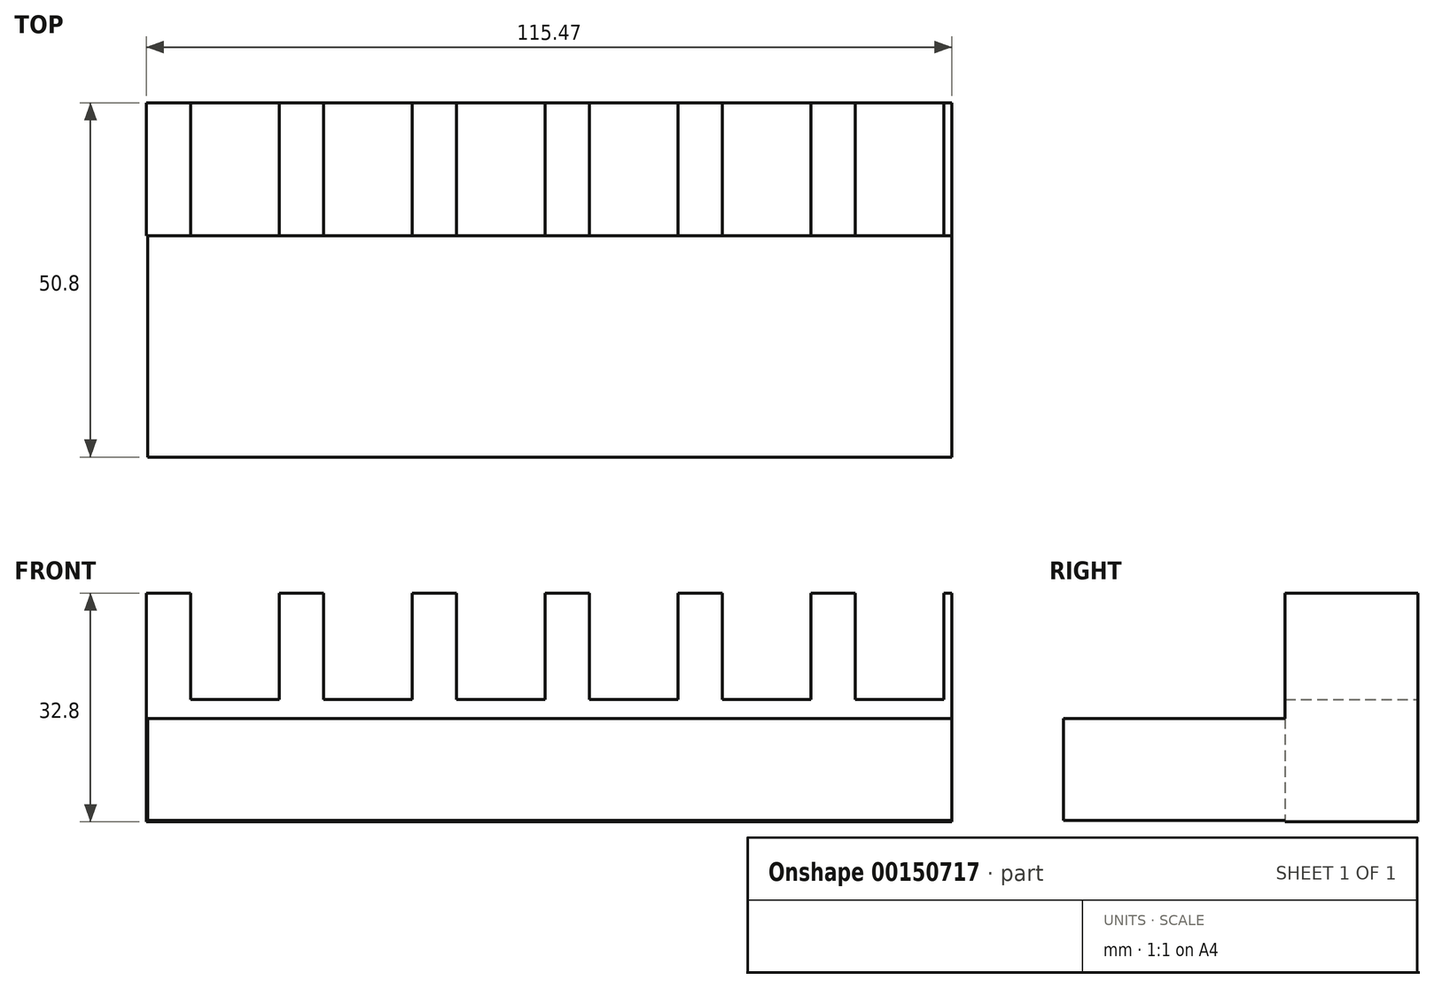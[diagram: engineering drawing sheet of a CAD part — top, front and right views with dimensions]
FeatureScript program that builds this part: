
annotation { "Feature Type Name" : "Feature", "Feature Type Description" : "" }
export const myFeature = defineFeature(function(context is Context, id is Id, definition is map)
    precondition{}
    {
        {
            var Q0;
            Q0=qCreatedBy(makeId("Front.planeOp"),FACE);
            var sketch = newSketch(context, id + "F0", { "sketchPlane" : qUnion([Q0])});
            skLineSegment(sketch, "E0.bottom", {"start": v(-57.62, 2.44) * mm, "end": v(57.85, 2.44) * mm});
            skLineSegment(sketch, "E0.top", {"start": v(-57.62, -30.36) * mm, "end": v(57.85, -30.36) * mm});
            skLineSegment(sketch, "E0.left", {"start": v(-57.62, 2.44) * mm, "end": v(-57.62, -30.36) * mm});
            skLineSegment(sketch, "E0.right", {"start": v(57.85, 2.44) * mm, "end": v(57.85, -30.36) * mm});
            skSolve(sketch);
        }
        {
            var Q0;
            Q0=makeQuery(id+"F0.imprint","IMPRINT",FACE,{"disambiguationData":[TD([[makeQuery(id+"F0.imprint","IMPRINT",EDGE,{"derivedFrom":sQuery(id+"F0.wireOp",EDGE,"E0.bottom")}),-1.0]])]});
            extrude(context, id + "F1", {"entities" : qUnion([Q0]), "depth" : 19.05 * mm});
        }
        {
            var Q0;
            Q0=qCreatedBy(makeId("Front.planeOp"),FACE);
            var sketch = newSketch(context, id + "F2", { "sketchPlane" : qUnion([Q0])});
            skLineSegment(sketch, "E1.bottom", {"start": v(-57.4, -30.14) * mm, "end": v(57.85, -30.14) * mm});
            skLineSegment(sketch, "E1.top", {"start": v(-57.4, -15.51) * mm, "end": v(57.85, -15.51) * mm});
            skLineSegment(sketch, "E1.left", {"start": v(-57.4, -30.14) * mm, "end": v(-57.4, -15.51) * mm});
            skLineSegment(sketch, "E1.right", {"start": v(57.85, -30.14) * mm, "end": v(57.85, -15.51) * mm});
            skSolve(sketch);
        }
        {
            var Q0;
            Q0 = qSketchRegion(id + "F2", true);
            extrude(context, id + "F3", {"entities" : qUnion([Q0]), "operationType" : NewBodyOperationType.ADD, "depth" : 50.8 * mm});
        }
        {
            var Q0;
            Q0=makeQuery(id+"F1.opExtrude","CAP_FACE",FACE,{"disambiguationData":[OSD([sQuery(id+"F0.wireOp",EDGE,"E0.bottom"),sQuery(id+"F0.wireOp",EDGE,"E0.top"),sQuery(id+"F0.wireOp",EDGE,"E0.left"),sQuery(id+"F0.wireOp",EDGE,"E0.right")])],"isStart":true});
            var sketch = newSketch(context, id + "F4", { "sketchPlane" : qUnion([Q0])});
            skLineSegment(sketch, "E2.bottom", {"start": v(51.27, 2.44) * mm, "end": v(38.57, 2.44) * mm});
            skLineSegment(sketch, "E2.top", {"start": v(51.27, -12.8) * mm, "end": v(38.57, -12.8) * mm});
            skLineSegment(sketch, "E2.left", {"start": v(51.27, 2.44) * mm, "end": v(51.27, -12.8) * mm});
            skLineSegment(sketch, "E2.right", {"start": v(38.57, 2.44) * mm, "end": v(38.57, -12.8) * mm});
            skLineSegment(sketch, "E3.bottom", {"start": v(32.22, 2.44) * mm, "end": v(19.52, 2.44) * mm});
            skLineSegment(sketch, "E3.top", {"start": v(32.22, -12.8) * mm, "end": v(19.52, -12.8) * mm});
            skLineSegment(sketch, "E3.left", {"start": v(32.22, 2.44) * mm, "end": v(32.22, -12.8) * mm});
            skLineSegment(sketch, "E3.right", {"start": v(19.52, 2.44) * mm, "end": v(19.52, -12.8) * mm});
            skLineSegment(sketch, "E4.bottom", {"start": v(13.17, 2.44) * mm, "end": v(0.47, 2.44) * mm});
            skLineSegment(sketch, "E4.top", {"start": v(13.17, -12.8) * mm, "end": v(0.47, -12.8) * mm});
            skLineSegment(sketch, "E4.left", {"start": v(13.17, 2.44) * mm, "end": v(13.17, -12.8) * mm});
            skLineSegment(sketch, "E4.right", {"start": v(0.47, 2.44) * mm, "end": v(0.47, -12.8) * mm});
            skLineSegment(sketch, "E5.bottom", {"start": v(-5.88, 2.44) * mm, "end": v(-18.58, 2.44) * mm});
            skLineSegment(sketch, "E5.top", {"start": v(-5.88, -12.8) * mm, "end": v(-18.58, -12.8) * mm});
            skLineSegment(sketch, "E5.left", {"start": v(-5.88, 2.44) * mm, "end": v(-5.88, -12.8) * mm});
            skLineSegment(sketch, "E5.right", {"start": v(-18.58, 2.44) * mm, "end": v(-18.58, -12.8) * mm});
            skLineSegment(sketch, "E6.bottom", {"start": v(-24.93, 2.44) * mm, "end": v(-37.63, 2.44) * mm});
            skLineSegment(sketch, "E6.top", {"start": v(-24.93, -12.8) * mm, "end": v(-37.63, -12.8) * mm});
            skLineSegment(sketch, "E6.left", {"start": v(-24.93, 2.44) * mm, "end": v(-24.93, -12.8) * mm});
            skLineSegment(sketch, "E6.right", {"start": v(-37.63, 2.44) * mm, "end": v(-37.63, -12.8) * mm});
            skLineSegment(sketch, "E7.bottom", {"start": v(-43.98, 2.44) * mm, "end": v(-56.68, 2.44) * mm});
            skLineSegment(sketch, "E7.top", {"start": v(-43.98, -12.8) * mm, "end": v(-56.68, -12.8) * mm});
            skLineSegment(sketch, "E7.left", {"start": v(-43.98, 2.44) * mm, "end": v(-43.98, -12.8) * mm});
            skLineSegment(sketch, "E7.right", {"start": v(-56.68, 2.44) * mm, "end": v(-56.68, -12.8) * mm});
            skSolve(sketch);
        }
        {
            var Q0;
            Q0=makeQuery(id+"F4.imprint","IMPRINT",FACE,{"disambiguationData":[TD([[makeQuery(id+"F4.imprint","IMPRINT",EDGE,{"derivedFrom":sQuery(id+"F4.wireOp",EDGE,"E2.bottom")}),1.0]])]});
            var Q1;
            Q1=makeQuery(id+"F4.imprint","IMPRINT",FACE,{"disambiguationData":[TD([[makeQuery(id+"F4.imprint","IMPRINT",EDGE,{"derivedFrom":sQuery(id+"F4.wireOp",EDGE,"E3.bottom")}),1.0]])]});
            var Q2;
            Q2=makeQuery(id+"F4.imprint","IMPRINT",FACE,{"disambiguationData":[TD([[makeQuery(id+"F4.imprint","IMPRINT",EDGE,{"derivedFrom":sQuery(id+"F4.wireOp",EDGE,"E4.bottom")}),1.0]])]});
            var Q3;
            Q3=makeQuery(id+"F4.imprint","IMPRINT",FACE,{"disambiguationData":[TD([[makeQuery(id+"F4.imprint","IMPRINT",EDGE,{"derivedFrom":sQuery(id+"F4.wireOp",EDGE,"E5.bottom")}),1.0]])]});
            var Q4;
            Q4=makeQuery(id+"F4.imprint","IMPRINT",FACE,{"disambiguationData":[TD([[makeQuery(id+"F4.imprint","IMPRINT",EDGE,{"derivedFrom":sQuery(id+"F4.wireOp",EDGE,"E6.bottom")}),1.0]])]});
            var Q5;
            Q5=makeQuery(id+"F4.imprint","IMPRINT",FACE,{"disambiguationData":[TD([[makeQuery(id+"F4.imprint","IMPRINT",EDGE,{"derivedFrom":sQuery(id+"F4.wireOp",EDGE,"E7.bottom")}),1.0]])]});
            extrude(context, id + "F5", {"entities" : qUnion([Q0, Q1, Q2, Q3, Q4, Q5]), "operationType" : NewBodyOperationType.REMOVE, "oppositeDirection" : true, "depth" : 19.05 * mm});
        }
    });
